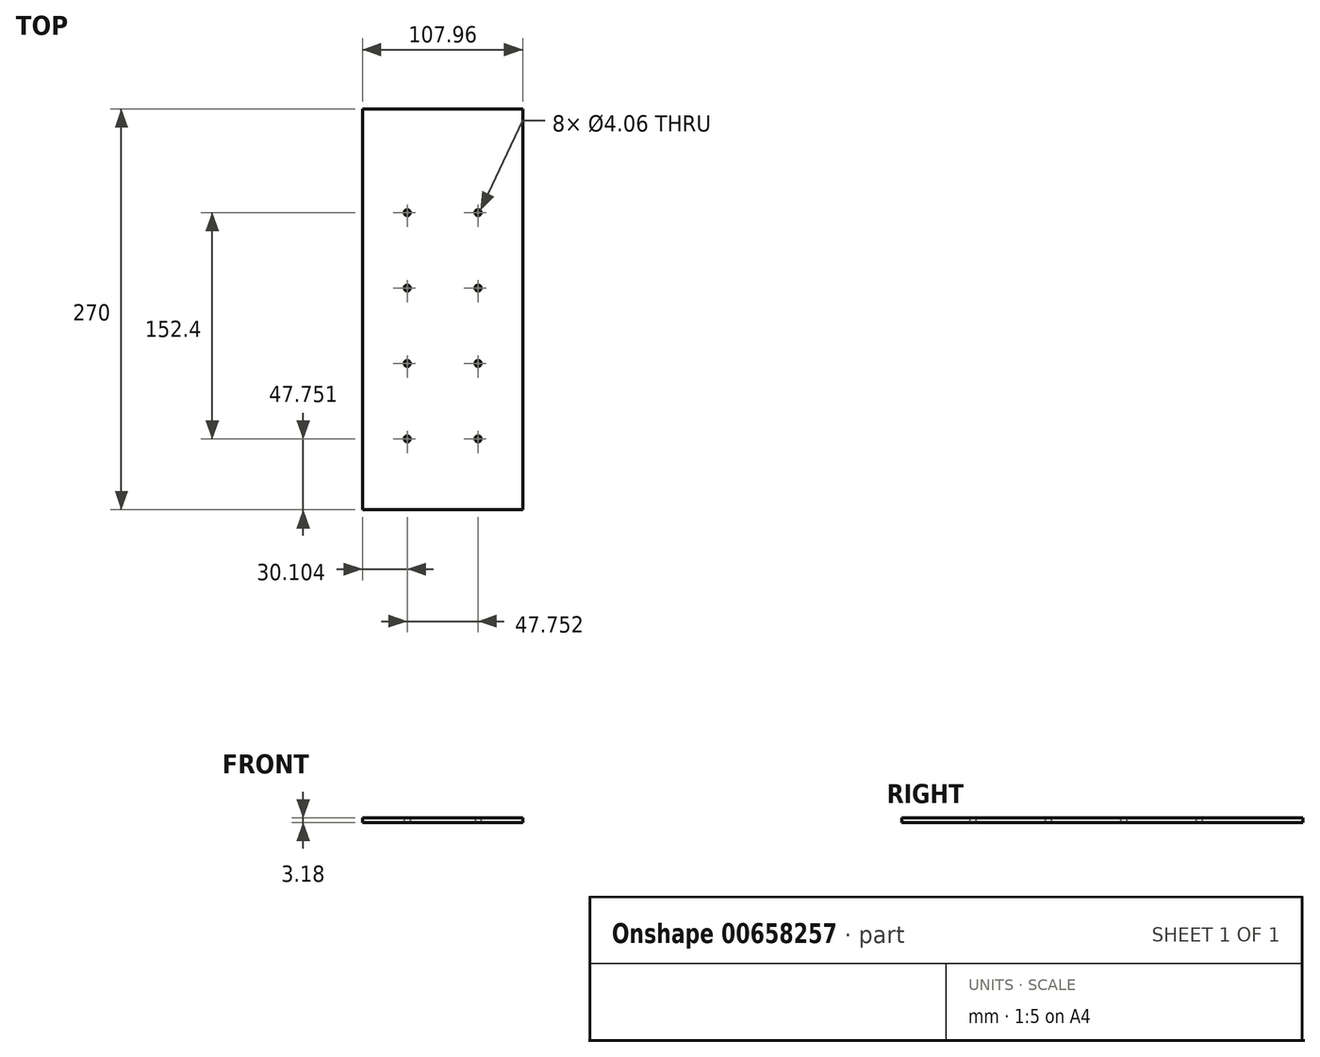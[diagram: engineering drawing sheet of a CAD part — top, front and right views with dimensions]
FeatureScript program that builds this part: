
annotation { "Feature Type Name" : "Feature", "Feature Type Description" : "" }
export const myFeature = defineFeature(function(context is Context, id is Id, definition is map)
    precondition{}
    {
        {
            var Q0;
            Q0=qCreatedBy(makeId("Top.planeOp"),FACE);
            var sketch = newSketch(context, id + "F0", { "sketchPlane" : qUnion([Q0])});
            skLineSegment(sketch, "E0.bottom", {"start": v(-53.97, 135) * mm, "end": v(53.98, 135) * mm});
            skLineSegment(sketch, "E0.top", {"start": v(-53.97, -135) * mm, "end": v(53.97, -135) * mm});
            skLineSegment(sketch, "E0.left", {"start": v(-53.98, 135) * mm, "end": v(-53.97, -135) * mm});
            skLineSegment(sketch, "E0.right", {"start": v(53.97, 135) * mm, "end": v(53.98, -135) * mm});
            skPoint(sketch, "E1", {"position": v(0, 135) * mm});
            skPoint(sketch, "E2", {"position": v(-53.97, 0) * mm});
            skLineSegment(sketch, "E3.bottom", {"start": v(-28.57, -117.07) * mm, "end": v(28.57, -117.07) * mm, "construction": true});
            skLineSegment(sketch, "E3.top", {"start": v(-28.58, 90.55) * mm, "end": v(28.58, 90.55) * mm, "construction": true});
            skLineSegment(sketch, "E3.left", {"start": v(-28.57, -117.07) * mm, "end": v(-28.58, 90.55) * mm, "construction": true});
            skLineSegment(sketch, "E3.right", {"start": v(28.58, -117.07) * mm, "end": v(28.57, 90.55) * mm, "construction": true});
            skPoint(sketch, "E4", {"position": v(0, -117.07) * mm});
            skLineSegment(sketch, "E5", {"start": v(-28.58, 65.15) * mm, "end": v(28.58, 65.15) * mm, "construction": true});
            skLineSegment(sketch, "E6", {"start": v(-28.58, 14.35) * mm, "end": v(28.58, 14.35) * mm, "construction": true});
            skLineSegment(sketch, "E7", {"start": v(-28.58, -36.45) * mm, "end": v(28.58, -36.45) * mm, "construction": true});
            skLineSegment(sketch, "E8", {"start": v(-28.58, -87.25) * mm, "end": v(28.58, -87.25) * mm, "construction": true});
            skCircle(sketch, "E9", {"center": v(23.88, 65.15) * mm, "radius": 2.03 * mm});
            skCircle(sketch, "E10", {"center": v(-23.88, 65.15) * mm, "radius": 2.03 * mm});
            skCircle(sketch, "E11", {"center": v(23.88, 14.35) * mm, "radius": 2.03 * mm});
            skCircle(sketch, "E12", {"center": v(-23.88, 14.35) * mm, "radius": 2.03 * mm});
            skPoint(sketch, "E12.centerSnap0", {"position": v(0, 14.35) * mm});
            skCircle(sketch, "E13", {"center": v(23.88, -36.45) * mm, "radius": 2.03 * mm});
            skCircle(sketch, "E14", {"center": v(-23.88, -36.45) * mm, "radius": 2.03 * mm});
            skCircle(sketch, "E15", {"center": v(23.88, -87.25) * mm, "radius": 2.03 * mm});
            skCircle(sketch, "E16", {"center": v(-23.88, -87.25) * mm, "radius": 2.03 * mm});
            skSolve(sketch);
        }
        {
            var Q0;
            Q0 = qSketchRegion(id + "F0", true);
            extrude(context, id + "F1", {"entities" : qUnion([Q0]), "depth" : 3.17 * mm, "offsetDistance" : 25.4 * mm});
        }
    });
